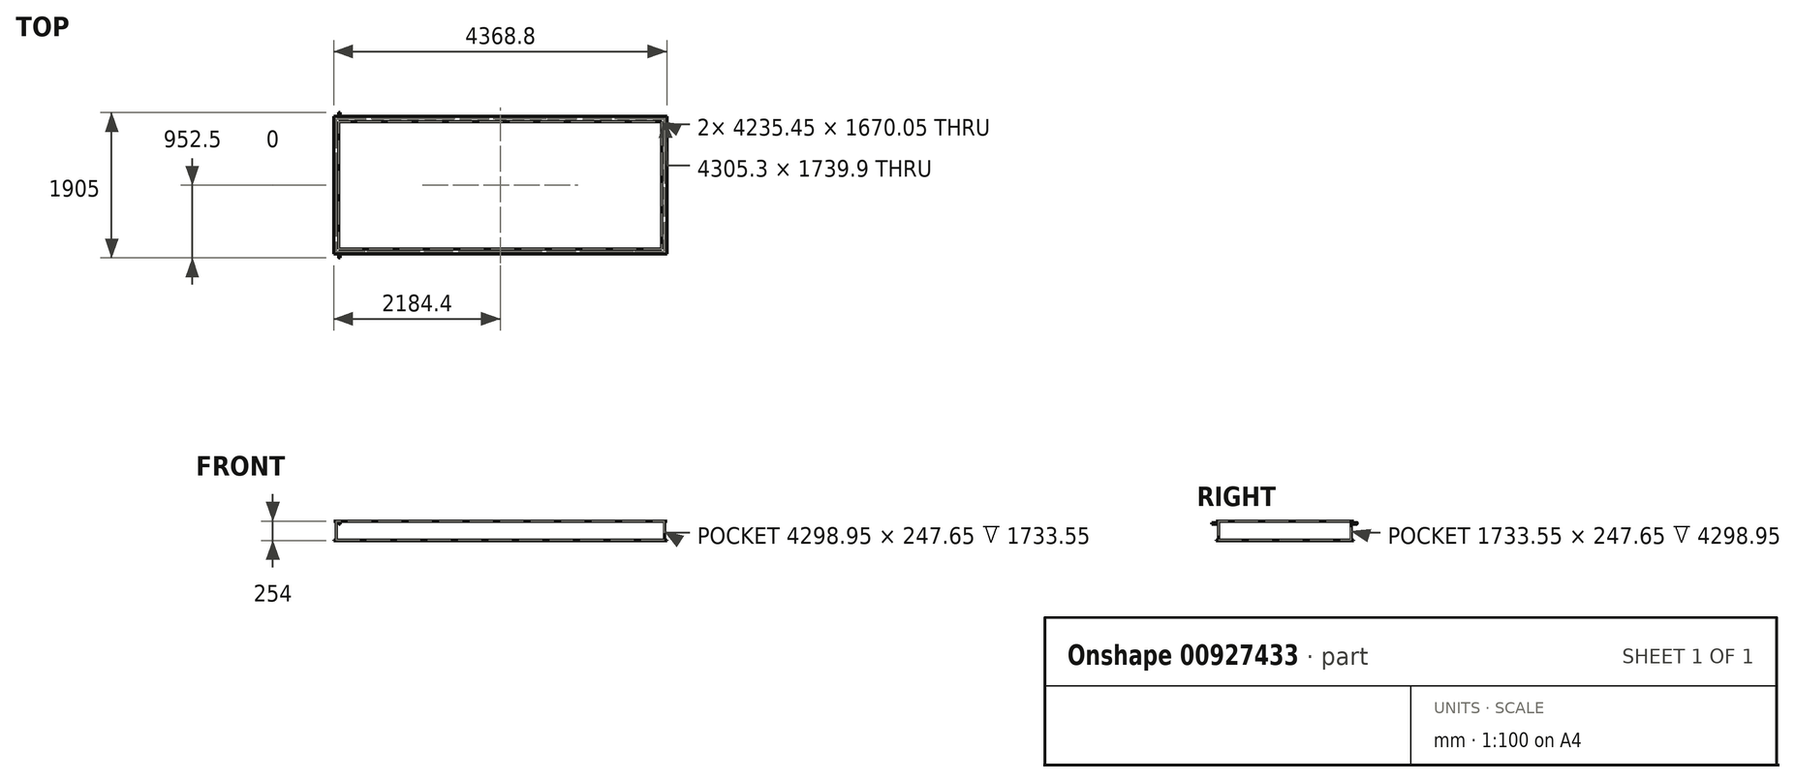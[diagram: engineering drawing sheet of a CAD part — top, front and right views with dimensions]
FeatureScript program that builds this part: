
annotation { "Feature Type Name" : "Feature", "Feature Type Description" : "" }
export const myFeature = defineFeature(function(context is Context, id is Id, definition is map)
    precondition{}
    {
        {
            var Q0;
            Q0=qCreatedBy(makeId("Top.planeOp"),FACE);
            var sketch = newSketch(context, id + "F0", { "sketchPlane" : qUnion([Q0])});
            skLineSegment(sketch, "E0", {"start": v(0, 0) * mm, "end": v(4368.8, 0) * mm});
            skLineSegment(sketch, "E1", {"start": v(4368.8, 0) * mm, "end": v(4368.8, 1803.4) * mm});
            skLineSegment(sketch, "E2", {"start": v(4368.8, 1803.4) * mm, "end": v(0, 1803.4) * mm});
            skLineSegment(sketch, "E3", {"start": v(0, 1803.4) * mm, "end": v(0, 0) * mm});
            skSolve(sketch);
        }
        {
            var Q0;
            Q0=qCreatedBy(makeId("Right.planeOp"),FACE);
            var sketch = newSketch(context, id + "F1", { "sketchPlane" : qUnion([Q0])});
            skLineSegment(sketch, "E4", {"start": v(0, 0) * mm, "end": v(66.68, 0) * mm});
            skLineSegment(sketch, "E5", {"start": v(66.68, 0) * mm, "end": v(66.68, -3.17) * mm});
            skLineSegment(sketch, "E6", {"start": v(66.68, -3.17) * mm, "end": v(34.93, -3.17) * mm});
            skLineSegment(sketch, "E7", {"start": v(34.93, -3.17) * mm, "end": v(34.93, -250.83) * mm});
            skLineSegment(sketch, "E8", {"start": v(34.93, -250.83) * mm, "end": v(66.68, -250.83) * mm});
            skLineSegment(sketch, "E9", {"start": v(66.68, -250.83) * mm, "end": v(66.68, -254) * mm});
            skLineSegment(sketch, "E10", {"start": v(66.68, -254) * mm, "end": v(0, -254) * mm});
            skLineSegment(sketch, "E11", {"start": v(0, -254) * mm, "end": v(0, -250.83) * mm});
            skLineSegment(sketch, "E12", {"start": v(0, -250.83) * mm, "end": v(31.75, -250.83) * mm});
            skLineSegment(sketch, "E13", {"start": v(31.75, -250.83) * mm, "end": v(31.75, -3.17) * mm});
            skLineSegment(sketch, "E14", {"start": v(31.75, -3.17) * mm, "end": v(0, -3.17) * mm});
            skLineSegment(sketch, "E15", {"start": v(0, -3.17) * mm, "end": v(0, 0) * mm});
            skSolve(sketch);
        }
        {
            var Q0;
            Q0 = qSketchRegion(id + "F1", true);
            var Q1;
            Q1 = qConstructionFilter(qBodyType(qCreatedBy(id + "F0" ,EDGE), BodyType.WIRE), ConstructionObject.NO);
            sweep(context, id + "F2", {"profiles" : qUnion([Q0]), "path" : qUnion([Q1])});
        }
        {
            var Q0;
            Q0=makeQuery(id+"F2.opSweep","SWEPT_FACE",FACE,{"disambiguationData":[OSD([sQuery(id+"F0.wireOp",EDGE,"E0"),sQuery(id+"F1.wireOp",EDGE,"E13")])]});
            var sketch = newSketch(context, id + "F3", { "sketchPlane" : qUnion([Q0])});
            skCircle(sketch, "E16", {"center": v(75, -30) * mm, "radius": 9.53 * mm});
            skSolve(sketch);
        }
        {
            var Q0;
            Q0 = qSketchRegion(id + "F3", true);
            extrude(context, id + "F4", {"entities" : qUnion([Q0]), "operationType" : NewBodyOperationType.ADD, "depth" : 82.55 * mm, "offsetDistance" : 25 * mm});
        }
        {
            var Q0;
            Q0=makeQuery(id+"F2.opSweep","SWEPT_FACE",FACE,{"disambiguationData":[OSD([sQuery(id+"F0.wireOp",EDGE,"E2"),sQuery(id+"F1.wireOp",EDGE,"E13")])]});
            var sketch = newSketch(context, id + "F5", { "sketchPlane" : qUnion([Q0])});
            skCircle(sketch, "E17", {"center": v(-75, -30) * mm, "radius": 9.53 * mm});
            skSolve(sketch);
        }
        {
            var Q0;
            Q0 = qSketchRegion(id + "F5", true);
            extrude(context, id + "F6", {"entities" : qUnion([Q0]), "operationType" : NewBodyOperationType.ADD, "depth" : 82.55 * mm, "offsetDistance" : 25 * mm});
        }
    });
